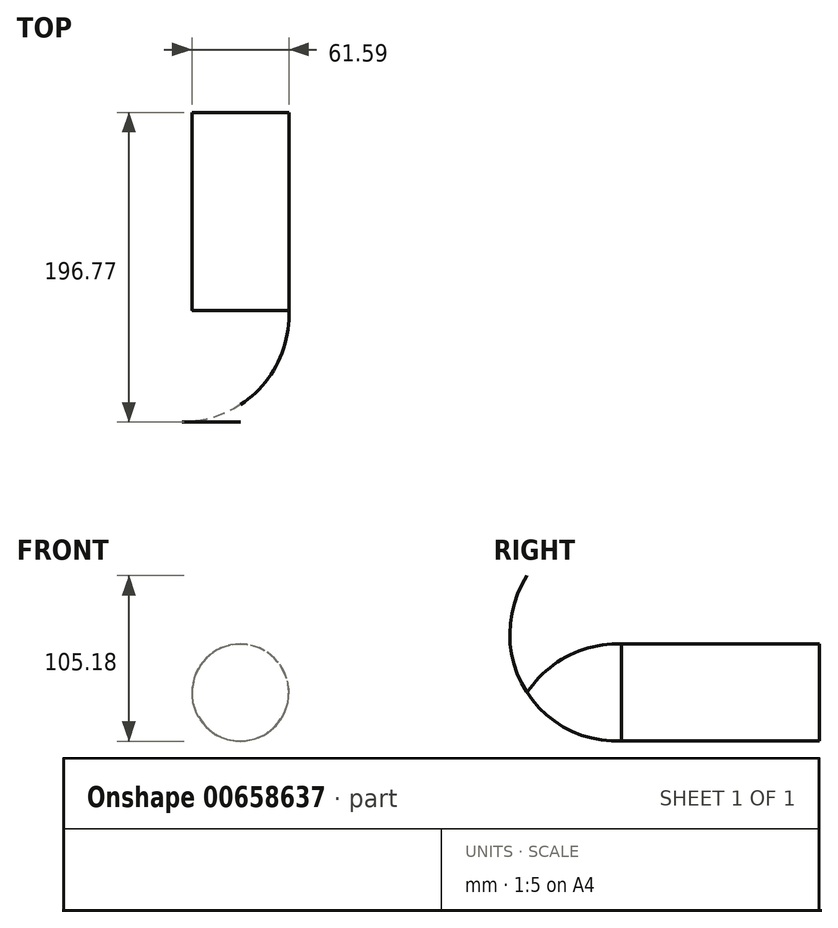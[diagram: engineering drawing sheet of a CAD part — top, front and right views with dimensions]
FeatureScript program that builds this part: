
annotation { "Feature Type Name" : "Feature", "Feature Type Description" : "" }
export const myFeature = defineFeature(function(context is Context, id is Id, definition is map)
    precondition{}
    {
        {
            var Q0;
            Q0=qCreatedBy(makeId("Top.planeOp"),FACE);
            var sketch = newSketch(context, id + "F0", { "sketchPlane" : qUnion([Q0])});
            skLineSegment(sketch, "E0", {"start": v(-34.82, 37.77) * mm, "end": v(-34.82, -22.23) * mm});
            skArc(sketch, "E1", {"start": v(-34.82, -22.23) * mm, "mid": v(-11.47, 3.69) * mm, "end": v(-4.03, 37.77) * mm});
            skLineSegment(sketch, "E2", {"start": v(-34.82, 46.34) * mm, "end": v(-34.82, -50.37) * mm, "construction": true});
            skLineSegment(sketch, "E3", {"start": v(-34.82, 37.77) * mm, "end": v(-4.03, 37.77) * mm});
            skSolve(sketch);
        }
        {
            var Q0;
            Q0=qSketchRegion(id+"F0",true);
            var Q1;
            Q1=sQuery(id+"F0.wireOp",EDGE,"E2");
            revolve(context, id + "F1", {"entities" : qUnion([Q0]), "axis" : qUnion([Q1]), "revolveType" : RevolveType.FULL});
        }
        {
            var Q0;
            Q0=makeQuery(id+"F1.opRevolve","SWEPT_FACE",FACE,{"disambiguationData":[OSD([sQuery(id+"F0.wireOp",EDGE,"E3")])]});
            var sketch = newSketch(context, id + "F2", { "sketchPlane" : qUnion([Q0])});
            skSolve(sketch);
        }
        {
            var Q0;
            Q0=makeQuery(id+"F2.imprint","IMPRINT",FACE,{"disambiguationData":[TD([[makeQuery(id+"F2.imprint","IMPRINT",EDGE,{"derivedFrom":makeQuery(id+"F1.opRevolve","SWEPT_EDGE",EDGE,{"disambiguationData":[OSD([sQuery(id+"F0.wireOp",EDGE,"E1"),sQuery(id+"F0.wireOp",EDGE,"E3")])]})}),1.0]])]});
            extrude(context, id + "F3", {"entities" : qUnion([Q0]), "depth" : 125.72 * mm, "offsetDistance" : 25 * mm});
        }
    });
